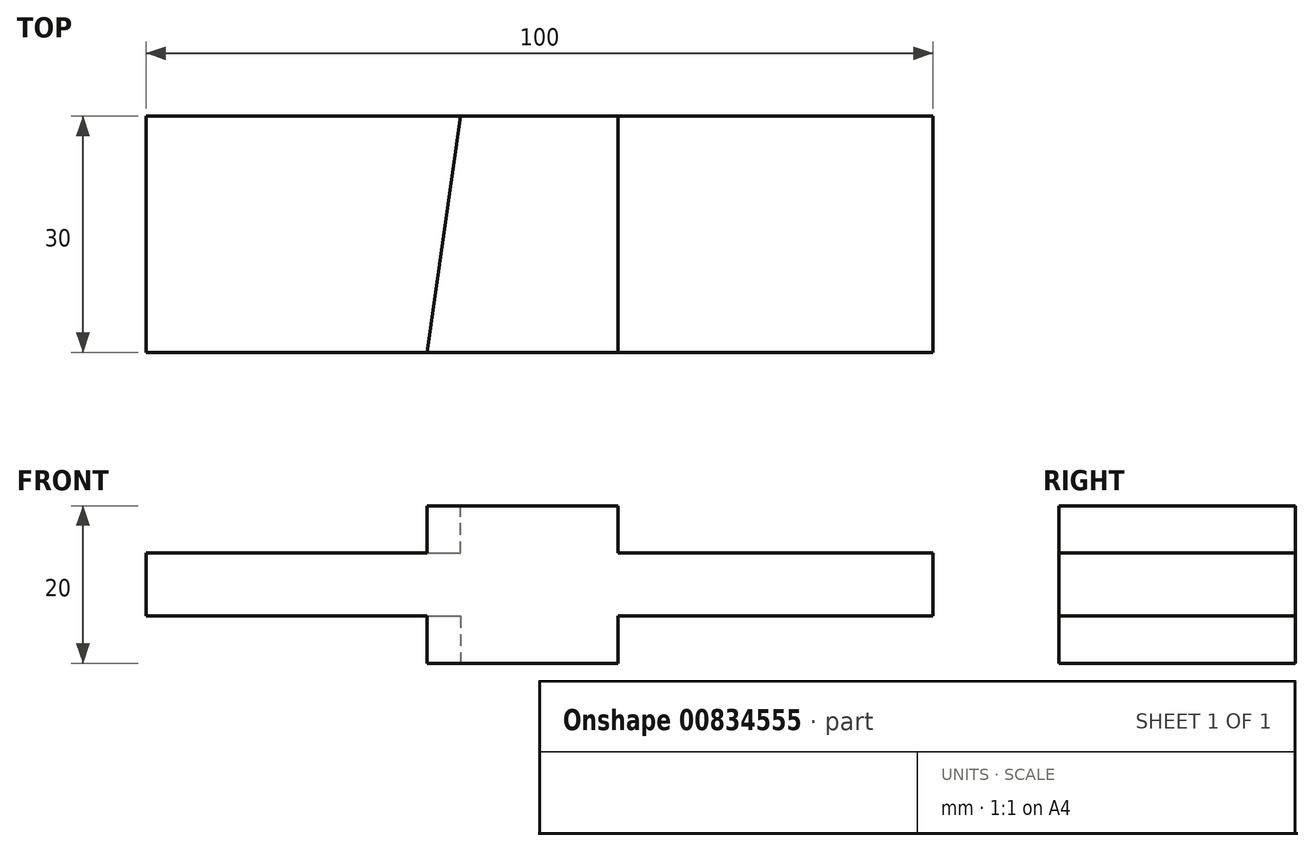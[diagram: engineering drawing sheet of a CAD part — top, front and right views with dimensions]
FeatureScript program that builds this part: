
annotation { "Feature Type Name" : "Feature", "Feature Type Description" : "" }
export const myFeature = defineFeature(function(context is Context, id is Id, definition is map)
    precondition{}
    {
        {
            var Q0;
            Q0=qCreatedBy(makeId("Top.planeOp"),FACE);
            var sketch = newSketch(context, id + "F0", { "sketchPlane" : qUnion([Q0])});
            skLineSegment(sketch, "E0.bottom", {"start": v(-47.52, -11.4) * mm, "end": v(52.48, -11.4) * mm});
            skLineSegment(sketch, "E0.top", {"start": v(-47.52, -41.4) * mm, "end": v(52.48, -41.4) * mm});
            skLineSegment(sketch, "E0.left", {"start": v(-47.52, -11.4) * mm, "end": v(-47.52, -41.4) * mm});
            skLineSegment(sketch, "E0.right", {"start": v(52.48, -11.4) * mm, "end": v(52.48, -41.4) * mm});
            skSolve(sketch);
        }
        {
            var Q0;
            Q0=makeQuery(id+"F0.imprint","IMPRINT",FACE,{"disambiguationData":[TD([[makeQuery(id+"F0.imprint","IMPRINT",EDGE,{"derivedFrom":sQuery(id+"F0.wireOp",EDGE,"E0.bottom")}),-1.0]])]});
            extrude(context, id + "F1", {"entities" : qUnion([Q0]), "depth" : 20 * mm, "offsetDistance" : 25 * mm});
        }
        {
            var Q0;
            Q0=makeQuery(id+"F1.opExtrude","CAP_FACE",FACE,{"disambiguationData":[OSD([sQuery(id+"F0.wireOp",EDGE,"E0.bottom"),sQuery(id+"F0.wireOp",EDGE,"E0.top"),sQuery(id+"F0.wireOp",EDGE,"E0.left"),sQuery(id+"F0.wireOp",EDGE,"E0.right")])],"isStart":false});
            var sketch = newSketch(context, id + "F2", { "sketchPlane" : qUnion([Q0])});
            skLineSegment(sketch, "E1", {"start": v(12.48, -11.4) * mm, "end": v(12.48, -41.4) * mm});
            skLineSegment(sketch, "E2", {"start": v(-11.8, -41.4) * mm, "end": v(-7.52, -11.4) * mm});
            skSolve(sketch);
        }
        {
            var Q0;
            Q0 = qSketchRegion(id + "F2", true);
            var Q1;
            {var subQ0=sQuery(id+"F2.wireOp",EDGE,"E2");Q1=makeQuery(id+"F2.imprint","IMPRINT",FACE,{"disambiguationData":[TD([[makeQuery(id+"F2.imprint","IMPRINT",EDGE,{"derivedFrom":subQ0}),1.0]])]});}
            var Q2;
            {var subQ0=sQuery(id+"F2.wireOp",EDGE,"E1");Q2=makeQuery(id+"F2.imprint","IMPRINT",FACE,{"disambiguationData":[TD([[makeQuery(id+"F2.imprint","IMPRINT",EDGE,{"derivedFrom":subQ0}),1.0]])]});}
            extrude(context, id + "F3", {"entities" : qUnion([Q0, Q1, Q2]), "operationType" : NewBodyOperationType.REMOVE, "oppositeDirection" : true, "depth" : 6 * mm, "offsetDistance" : 25 * mm});
        }
        {
            var Q0;
            Q0=makeQuery(id+"F1.opExtrude","CAP_FACE",FACE,{"disambiguationData":[OSD([sQuery(id+"F0.wireOp",EDGE,"E0.bottom"),sQuery(id+"F0.wireOp",EDGE,"E0.top"),sQuery(id+"F0.wireOp",EDGE,"E0.left"),sQuery(id+"F0.wireOp",EDGE,"E0.right")])],"isStart":true});
            var sketch = newSketch(context, id + "F4", { "sketchPlane" : qUnion([Q0])});
            skLineSegment(sketch, "E3", {"start": v(12.48, 41.4) * mm, "end": v(12.48, 11.4) * mm});
            skLineSegment(sketch, "E4", {"start": v(-11.8, 41.4) * mm, "end": v(-7.52, 11.4) * mm});
            skSolve(sketch);
        }
        {
            var Q0;
            Q0 = qSketchRegion(id + "F4", true);
            var Q1;
            {var subQ0=sQuery(id+"F4.wireOp",EDGE,"E4");Q1=makeQuery(id+"F4.imprint","IMPRINT",FACE,{"disambiguationData":[TD([[makeQuery(id+"F4.imprint","IMPRINT",EDGE,{"derivedFrom":subQ0}),-1.0]])]});}
            var Q2;
            {var subQ0=sQuery(id+"F4.wireOp",EDGE,"E3");Q2=makeQuery(id+"F4.imprint","IMPRINT",FACE,{"disambiguationData":[TD([[makeQuery(id+"F4.imprint","IMPRINT",EDGE,{"derivedFrom":subQ0}),1.0]])]});}
            extrude(context, id + "F5", {"entities" : qUnion([Q0, Q1, Q2]), "operationType" : NewBodyOperationType.REMOVE, "oppositeDirection" : true, "depth" : 6 * mm, "offsetDistance" : 25 * mm});
        }
    });
